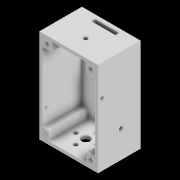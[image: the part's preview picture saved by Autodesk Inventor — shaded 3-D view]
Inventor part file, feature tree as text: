
AUTODESK INVENTOR PART (.ipt)
format: ipt  version: 2020 (Build 240168000, 168)  size: 224,768 bytes
history: native  units: mm
features: sketch x10, hole x6, extrude x4, projected_geometry x4, pattern_circular x1, fillet x1
ambient origin geometry x8: Origin, YZ Plane, XZ Plane, XY Plane, X Axis, Y Axis, Z Axis, Center Point
bodies: Solid1 (feature_tree)
feature tree (26):
  extrude  "Extrusion1"  Depth=79.0mm
  extrude  "Extrusion2"  Depth=2.5mm
  hole  "Hole1"  [1 undecoded]
  hole  "Hole2"  [1 undecoded]
  pattern_circular  "Circular Pattern1"  Count=4 Angle=360.0deg
  hole  "Hole3"  [1 undecoded]
  fillet  "Fillet3"  Radius=30.48mm
  hole  "Hole4"  [1 undecoded]
  extrude  "Extrusion3"  Depth=2.0mm
  hole  "Hole5"  [1 undecoded]
  hole  "Hole6"  [1 undecoded]
  extrude  "Extrusion4"  Depth=76.5mm
  sketch  "Sketch1"  dims[d0=49.5mm d1=79.0mm]
  sketch  "Sketch2"  dims[d2=35.867mm d3=0.0mm d4=2.5mm]
  sketch  "Sketch3"  dims[d5=2.5mm d6=2.5mm]
  projected_geometry  "Projected Loop1"
  sketch  "Sketch4"  dims[d7=2.5mm d8=32.367mm d9=0.0mm]
  projected_geometry  "Projected Loop2"
  sketch  "Sketch5"  dims[d12=17.367mm]
  sketch  "Sketch6"  dims[d13=7.1mm d14=6.0mm d15=4.0mm d16=2.0mm d17=90.0deg d18=8.0mm d19=20.594885mm]
  sketch  "Sketch7"  dims[d20=8.5mm]
  sketch  "Sketch8"  dims[d21=3.3mm d22=6.0mm d23=4.0mm d24=2.0mm d25=90.0deg d26=8.0mm d27=20.594885mm d28=40.0mm d29=360.0deg]
  projected_geometry  "Projected Loop3"
  sketch  "Sketch9"  dims[d31=21.75mm d32=2.986mm d33=30.48mm]
  sketch  "Sketch10"  dims[d34=22.86mm d35=22.952888mm d36=2.184mm d37=6.0mm d38=4.0mm d39=2.0mm d40=90.0deg d41=8.0mm d42=20.594885mm d43=2.0mm d44=30.0mm d47=26.0mm d48=3.0mm d49=6.0mm d50=4.0mm d51=2.0mm d52=90.0deg d53=8.0mm d54=20.594885mm d55=3.2mm d56=16.0mm d57=10.0mm d58=8.0mm d59=10.0mm d60=10.0mm d61=10.0mm d62=10.0mm d63=10.0mm d64=10.0mm d66=28.5mm d67=0.0mm d68=3.3mm d69=6.0mm d70=4.0mm d71=2.0mm d72=90.0deg d73=8.0mm d74=20.594885mm d75=14.228mm d76=3.3mm d77=6.0mm d78=4.0mm d79=2.0mm d80=90.0deg d81=8.0mm d82=20.594885mm d83=20.0mm d84=3.0mm d85=76.5mm d86=0.0mm]
  projected_geometry  "Projected Loop4"
note: 6 required parameter values undecoded (feature->parameter linkage not recoverable at this tier; creation-order binding heuristic only, values carry confidence <= 0.55)
